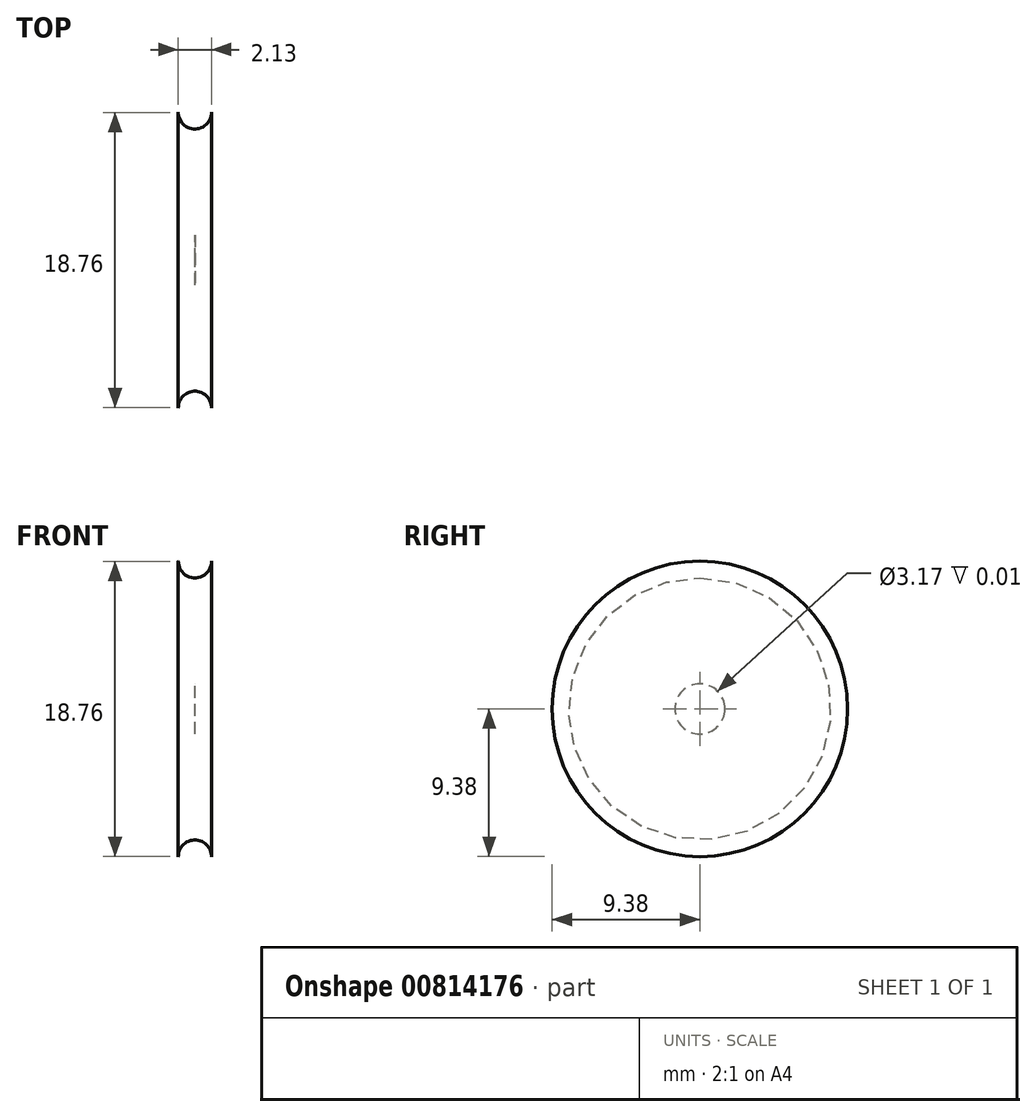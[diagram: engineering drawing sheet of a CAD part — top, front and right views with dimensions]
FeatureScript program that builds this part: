
annotation { "Feature Type Name" : "Feature", "Feature Type Description" : "" }
export const myFeature = defineFeature(function(context is Context, id is Id, definition is map)
    precondition{}
    {
        {
            var Q0;
            Q0=qCreatedBy(makeId("Front.planeOp"),FACE);
            var sketch = newSketch(context, id + "F0", { "sketchPlane" : qUnion([Q0])});
            skCircle(sketch, "E0", {"center": v(0, -0.08) * mm, "radius": 9.53 * mm});
            skLineSegment(sketch, "E1.bottom", {"start": v(-1.07, 0) * mm, "end": v(1.06, 0) * mm});
            skLineSegment(sketch, "E1.top", {"start": v(-1.07, 9.38) * mm, "end": v(1.06, 9.38) * mm});
            skLineSegment(sketch, "E1.left", {"start": v(-1.07, 0) * mm, "end": v(-1.07, 9.38) * mm});
            skLineSegment(sketch, "E1.right", {"start": v(1.06, 0) * mm, "end": v(1.06, 9.38) * mm});
            skCircle(sketch, "E2", {"center": v(0, 9.38) * mm, "radius": 1.06 * mm});
            skSolve(sketch);
        }
        {
            var Q0;
            {var subQ1=sQuery(id+"F0.wireOp",EDGE,"E1.bottom");Q0=makeQuery(id+"F0.imprint","IMPRINT",FACE,{"disambiguationData":[TD([[makeQuery(id+"F0.imprint","IMPRINT",EDGE,{"derivedFrom":subQ1}),1.0]])]});}
            var Q1;
            Q1=sQuery(id+"F0.wireOp",EDGE,"E1.bottom");
            revolve(context, id + "F1", {"surfaceOperationType" : NewSurfaceOperationType.NEW, "entities" : qUnion([Q0]), "axis" : qUnion([Q1]), "revolveType" : RevolveType.FULL});
        }
        {
            var Q0;
            Q0=qCreatedBy(makeId("Right.planeOp"),FACE);
            var sketch = newSketch(context, id + "F2", { "sketchPlane" : qUnion([Q0])});
            skCircle(sketch, "E3", {"center": v(0, 0) * mm, "radius": 1.59 * mm});
            skSolve(sketch);
        }
        {
            var Q0;
            Q0 = qSketchRegion(id + "F2", true);
            extrude(context, id + "F3", {"entities" : qUnion([Q0]), "operationType" : NewBodyOperationType.REMOVE, "endBound" : BoundingType.SYMMETRIC, "depth" : 1 / 101.6 * mm, "offsetDistance" : 25 * mm});
        }
    });
